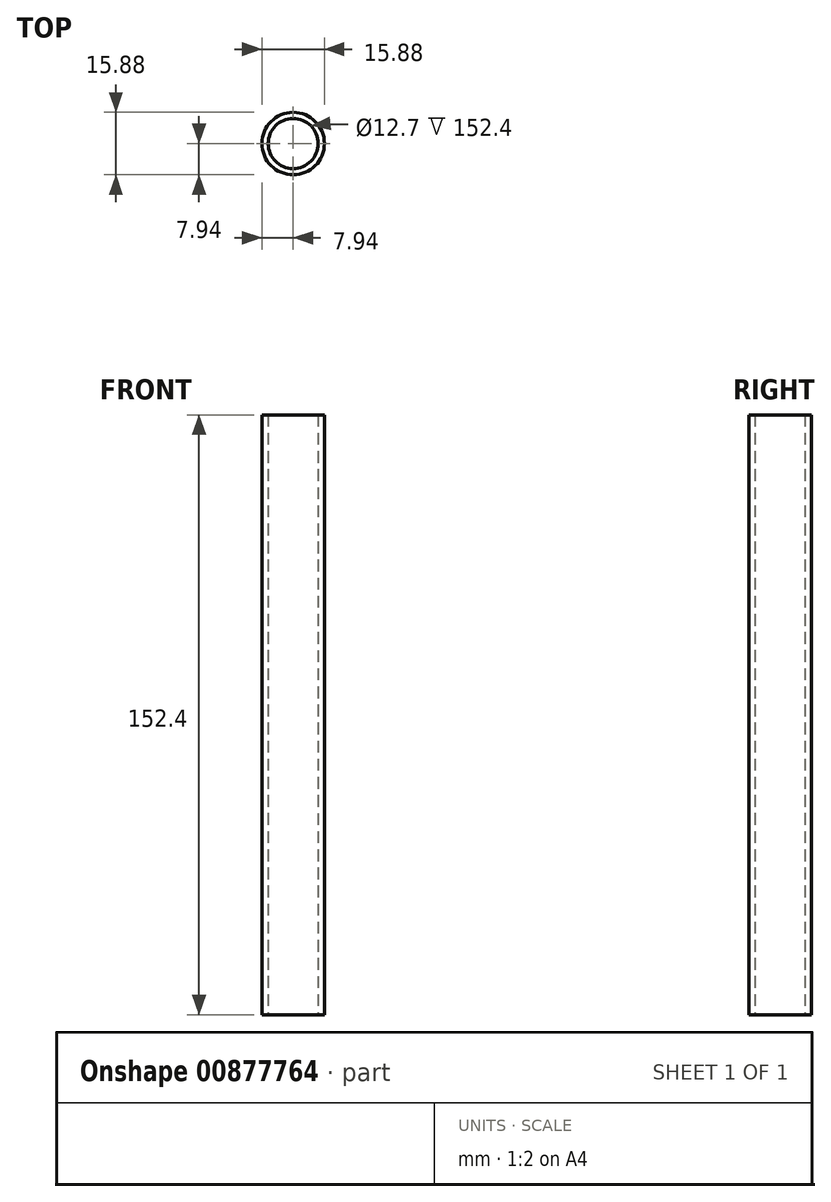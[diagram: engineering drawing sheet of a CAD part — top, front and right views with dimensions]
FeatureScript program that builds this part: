
annotation { "Feature Type Name" : "Feature", "Feature Type Description" : "" }
export const myFeature = defineFeature(function(context is Context, id is Id, definition is map)
    precondition{}
    {
        {
            var Q0;
            Q0=qCreatedBy(makeId("Top.planeOp"),FACE);
            var sketch = newSketch(context, id + "F0", { "sketchPlane" : qUnion([Q0])});
            skCircle(sketch, "E0", {"center": v(0, 0) * mm, "radius": 6.35 * mm});
            skCircle(sketch, "E1.0", {"center": v(0, 0) * mm, "radius": 7.94 * mm});
            skSolve(sketch);
        }
        {
            var Q0;
            Q0 = qSketchRegion(id + "F0", true);
            extrude(context, id + "F1", {"entities" : qUnion([Q0]), "depth" : 152.4 * mm, "offsetDistance" : 25.4 * mm});
        }
    });
